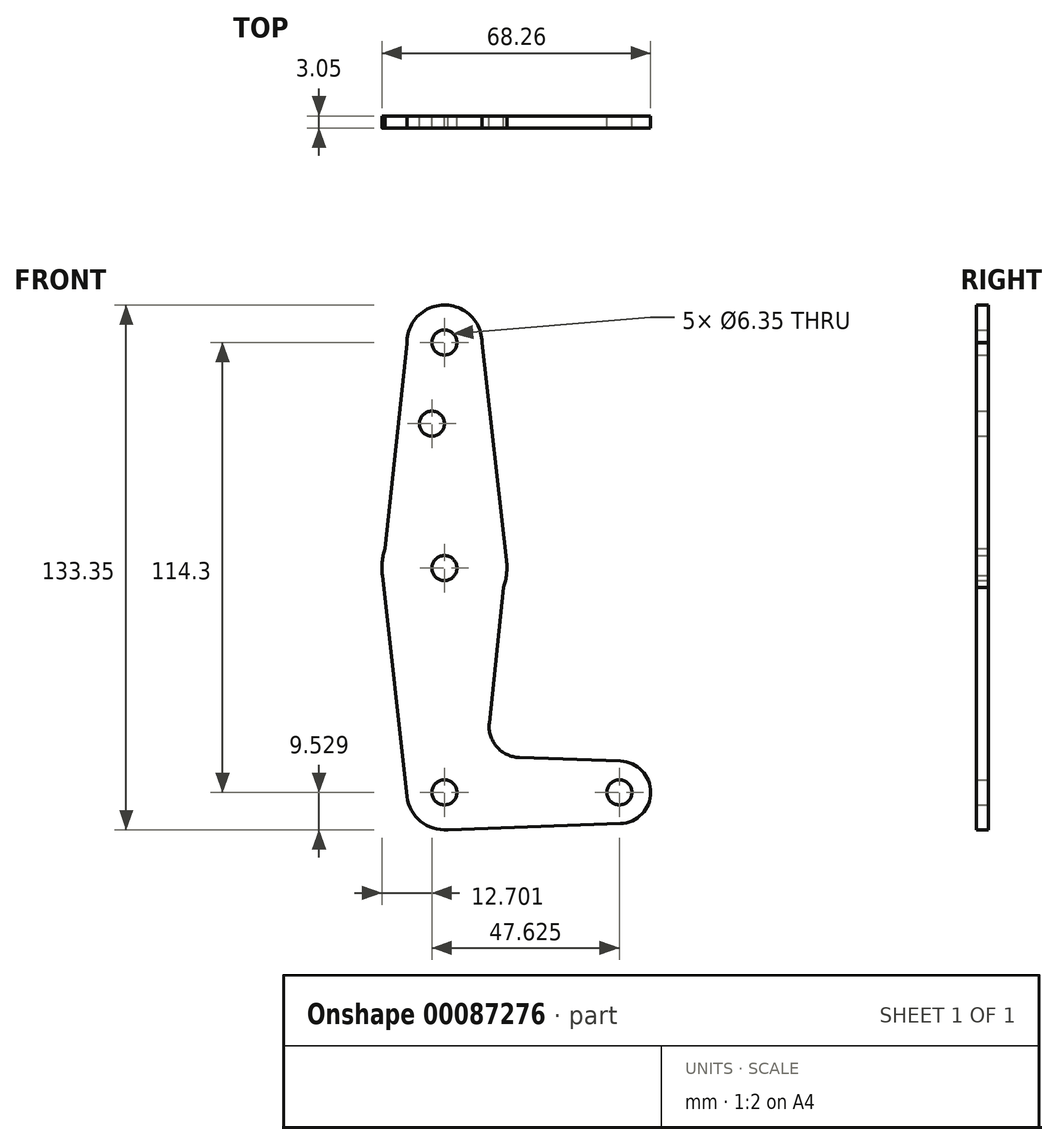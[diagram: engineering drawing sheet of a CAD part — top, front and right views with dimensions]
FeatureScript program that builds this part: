
annotation { "Feature Type Name" : "Feature", "Feature Type Description" : "" }
export const myFeature = defineFeature(function(context is Context, id is Id, definition is map)
    precondition{}
    {
        {
            var Q0;
            Q0=qCreatedBy(makeId("Front.planeOp"),FACE);
            var sketch = newSketch(context, id + "F0", { "sketchPlane" : qUnion([Q0])});
            skCircle(sketch, "E0", {"center": v(-19.93, 93.02) * mm, "radius": 9.53 * mm});
            skLineSegment(sketch, "E1", {"start": v(-19.93, 93.02) * mm, "end": v(-19.93, -21.28) * mm, "construction": true});
            skLineSegment(sketch, "E2", {"start": v(-19.93, -21.28) * mm, "end": v(24.52, -21.28) * mm, "construction": true});
            skCircle(sketch, "E3", {"center": v(-19.93, 35.87) * mm, "radius": 15.88 * mm});
            skCircle(sketch, "E4", {"center": v(-19.93, -21.28) * mm, "radius": 9.53 * mm});
            skCircle(sketch, "E5", {"center": v(24.52, -21.28) * mm, "radius": 7.94 * mm});
            skLineSegment(sketch, "E6", {"start": v(-29.45, 92.72) * mm, "end": v(-35.74, 34.43) * mm});
            skLineSegment(sketch, "E7", {"start": v(-35.74, 34.43) * mm, "end": v(-29.4, -22.34) * mm});
            skLineSegment(sketch, "E8", {"start": v(-10.4, 93.02) * mm, "end": v(-4.16, 37.65) * mm});
            skLineSegment(sketch, "E9", {"start": v(-4.16, 37.65) * mm, "end": v(-8.54, -3.65) * mm});
            skLineSegment(sketch, "E10", {"start": v(-0.92, -12.43) * mm, "end": v(24.8, -13.35) * mm});
            skLineSegment(sketch, "E11", {"start": v(-20.12, -30.8) * mm, "end": v(24.8, -29.21) * mm});
            skCircle(sketch, "E12", {"center": v(24.52, -21.28) * mm, "radius": 3.17 * mm});
            skCircle(sketch, "E13", {"center": v(-23.1, 72.4) * mm, "radius": 3.17 * mm});
            skCircle(sketch, "E14", {"center": v(-19.93, -21.28) * mm, "radius": 3.17 * mm});
            skCircle(sketch, "E15", {"center": v(-19.93, 93.02) * mm, "radius": 3.17 * mm});
            skArc(sketch, "E16.filletArc", {"start": v(-8.54, -3.65) * mm, "mid": v(-6.64, -9.7) * mm, "end": v(-0.92, -12.43) * mm});
            skCircle(sketch, "E17", {"center": v(-19.95, 35.7) * mm, "radius": 3.17 * mm});
            skSolve(sketch);
        }
        {
            var Q0;
            Q0 = qSketchRegion(id + "F0", true);
            extrude(context, id + "F1", {"entities" : qUnion([Q0]), "depth" : 3.05 * mm});
        }
    });
